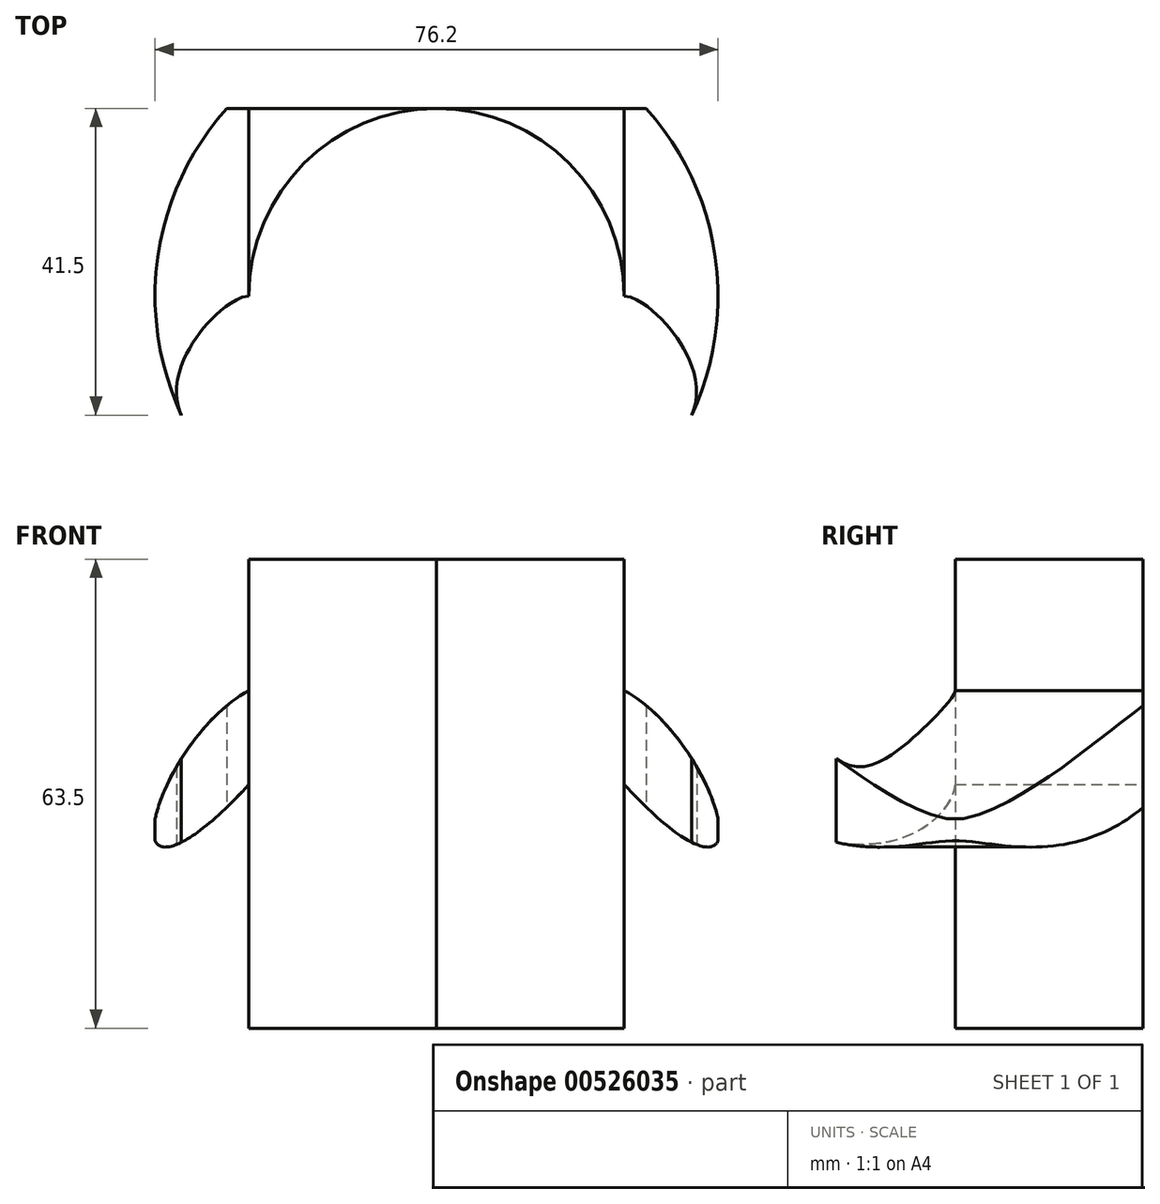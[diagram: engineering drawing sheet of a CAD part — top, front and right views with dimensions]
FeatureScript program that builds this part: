
annotation { "Feature Type Name" : "Feature", "Feature Type Description" : "" }
export const myFeature = defineFeature(function(context is Context, id is Id, definition is map)
    precondition{}
    {
        {
            var Q0;
            Q0=qCreatedBy(makeId("Front.planeOp"),FACE);
            var sketch = newSketch(context, id + "F0", { "sketchPlane" : qUnion([Q0])});
            skLineSegment(sketch, "E0", {"start": v(0, 0) * mm, "end": v(25.4, 0) * mm});
            skLineSegment(sketch, "E1", {"start": v(25.4, 0) * mm, "end": v(25.4, 63.5) * mm, "construction": true});
            skLineSegment(sketch, "E2", {"start": v(0, 0) * mm, "end": v(0, 88.9) * mm});
            skLineSegment(sketch, "E3", {"start": v(25.4, 63.5) * mm, "end": v(0, 63.5) * mm, "construction": true});
            skArc(sketch, "E4", {"start": v(25.4, 63.5) * mm, "mid": v(17.96, 81.46) * mm, "end": v(0, 88.9) * mm});
            skLineSegment(sketch, "E5", {"start": v(25.4, 63.5) * mm, "end": v(38.1, 63.5) * mm});
            skLineSegment(sketch, "E6", {"start": v(38.1, 63.5) * mm, "end": v(38.1, 0) * mm});
            skLineSegment(sketch, "E7", {"start": v(38.1, 0) * mm, "end": v(25.4, 0) * mm});
            skSolve(sketch);
        }
        {
            var Q0;
            Q0=makeQuery(id+"F0.imprint","IMPRINT",FACE,{"disambiguationData":[TD([[makeQuery(id+"F0.imprint","IMPRINT",EDGE,{"derivedFrom":sQuery(id+"F0.wireOp",EDGE,"E0")}),1.0]])]});
            var Q1;
            Q1=sQuery(id+"F0.wireOp",EDGE,"E2");
            revolve(context, id + "F1", {"entities" : qUnion([Q0]), "axis" : qUnion([Q1]), "revolveType" : RevolveType.FULL});
        }
        {
            var Q0;
            Q0=qCreatedBy(makeId("Top.planeOp"),FACE);
            var sketch = newSketch(context, id + "F2", { "sketchPlane" : qUnion([Q0])});
            skArc(sketch, "E8.0", {"start": v(-25.4, 0) * mm, "mid": v(0, 25.4) * mm, "end": v(25.4, 0) * mm});
            skPoint(sketch, "E9.0", {"position": v(38.1, 0) * mm});
            skCircle(sketch, "E10", {"center": v(0, 0) * mm, "radius": 38.1 * mm});
            skLineSegment(sketch, "E11", {"start": v(0, 0) * mm, "end": v(38.1, 0) * mm, "construction": true});
            skLineSegment(sketch, "E12", {"start": v(0, 0) * mm, "end": v(34.53, -16.1) * mm, "construction": true});
            skLineSegment(sketch, "E13.MirrorCS", {"start": v(0, 0) * mm, "end": v(-34.53, -16.1) * mm, "construction": true});
            skLineSegment(sketch, "E14.MirrorCS", {"start": v(0, 0) * mm, "end": v(-38.1, 0) * mm, "construction": true});
            skFitSpline(sketch, "E15", {"points": [v(25.4, 0) * mm, v(34.53, -16.1) * mm], "startDerivative": vector(10.3, 0) * mm, "endDerivative": vector(-9.48, -20.34) * mm});
            skLineSegment(sketch, "E16", {"start": v(34.53, -16.1) * mm, "end": v(52.17, 21.72) * mm, "construction": true});
            skFitSpline(sketch, "E17.MirrorCS", {"points": [v(16.33, -19.46) * mm, v(34.53, -16.1) * mm], "startDerivative": vector(6.62, -7.9) * mm, "endDerivative": vector(9.48, 20.34) * mm});
            skFitSpline(sketch, "E18.MirrorCS", {"points": [v(-16.33, -19.46) * mm, v(-34.53, -16.1) * mm], "startDerivative": vector(-6.62, -7.9) * mm, "endDerivative": vector(-9.48, 20.34) * mm});
            skFitSpline(sketch, "E19.MirrorCS", {"points": [v(-25.4, 0) * mm, v(-34.53, -16.1) * mm], "startDerivative": vector(-10.3, 0) * mm, "endDerivative": vector(9.48, -20.34) * mm});
            skArc(sketch, "E20.trimOffspring", {"start": v(16.33, -19.46) * mm, "mid": v(0, -25.4) * mm, "end": v(-16.33, -19.46) * mm});
            skSolve(sketch);
        }
        {
            var Q0;
            Q0=makeQuery(id+"F2.imprint","IMPRINT",FACE,{"disambiguationData":[TD([[makeQuery(id+"F2.imprint","IMPRINT",EDGE,{"derivedFrom":sQuery(id+"F2.wireOp",EDGE,"E8.0")}),-1.0]])]});
            extrude(context, id + "F3", {"entities" : qUnion([Q0]), "operationType" : NewBodyOperationType.INTERSECT, "depth" : 101.6 * mm, "offsetDistance" : 25.4 * mm});
        }
        {
            var Q0;
            Q0=qCreatedBy(makeId("Front.planeOp"),FACE);
            var sketch = newSketch(context, id + "F4", { "sketchPlane" : qUnion([Q0])});
            skLineSegment(sketch, "E21", {"start": v(0, 0) * mm, "end": v(-25.4, 0) * mm});
            skLineSegment(sketch, "E22", {"start": v(-25.4, 0) * mm, "end": v(-38.1, 0) * mm, "construction": true});
            skLineSegment(sketch, "E23", {"start": v(0, 0) * mm, "end": v(0, 63.5) * mm, "construction": true});
            skLineSegment(sketch, "E24", {"start": v(0, 63.5) * mm, "end": v(-38.1, 63.5) * mm, "construction": true});
            skLineSegment(sketch, "E25", {"start": v(-38.1, 0) * mm, "end": v(-38.1, 25.4) * mm, "construction": true});
            skLineSegment(sketch, "E26", {"start": v(-25.4, 0) * mm, "end": v(-25.4, 33.02) * mm});
            skLineSegment(sketch, "E27", {"start": v(-25.4, 45.72) * mm, "end": v(-25.4, 63.5) * mm});
            skLineSegment(sketch, "E28", {"start": v(-25.4, 33.02) * mm, "end": v(-25.4, 45.72) * mm, "construction": true});
            skLineSegment(sketch, "E29", {"start": v(-38.1, 25.4) * mm, "end": v(-38.1, 63.5) * mm, "construction": true});
            skFitSpline(sketch, "E30", {"points": [v(-25.4, 45.72) * mm, v(-38.1, 25.4) * mm, v(-25.4, 33.02) * mm], "startDerivative": vector(-45.4, -25.38) * mm, "endDerivative": vector(43.5, 48.34) * mm});
            skLineSegment(sketch, "E31.MirrorCS", {"start": v(25.4, 0) * mm, "end": v(25.4, 33.02) * mm});
            skLineSegment(sketch, "E32.MirrorCS", {"start": v(25.4, 45.72) * mm, "end": v(25.4, 63.5) * mm});
            skFitSpline(sketch, "E33.MirrorCS", {"points": [v(25.4, 45.72) * mm, v(38.1, 25.4) * mm, v(25.4, 33.02) * mm], "startDerivative": vector(45.4, -25.38) * mm, "endDerivative": vector(-43.5, 48.34) * mm});
            skLineSegment(sketch, "E34.MirrorCS", {"start": v(0, 0) * mm, "end": v(25.4, 0) * mm});
            skArc(sketch, "E35", {"start": v(25.4, 63.5) * mm, "mid": v(0, 88.9) * mm, "end": v(-25.4, 63.5) * mm});
            skSolve(sketch);
        }
        {
            var Q0;
            Q0=makeQuery(id+"F4.imprint","IMPRINT",FACE,{"disambiguationData":[TD([[makeQuery(id+"F4.imprint","IMPRINT",EDGE,{"derivedFrom":sQuery(id+"F4.wireOp",EDGE,"E21")}),-1.0]])]});
            extrude(context, id + "F5", {"entities" : qUnion([Q0]), "operationType" : NewBodyOperationType.INTERSECT, "depth" : 25.4 * mm, "offsetDistance" : 25.4 * mm, "hasSecondDirection" : true, "secondDirectionOppositeDirection" : true, "secondDirectionDepth" : 25.4 * mm});
        }
    });
